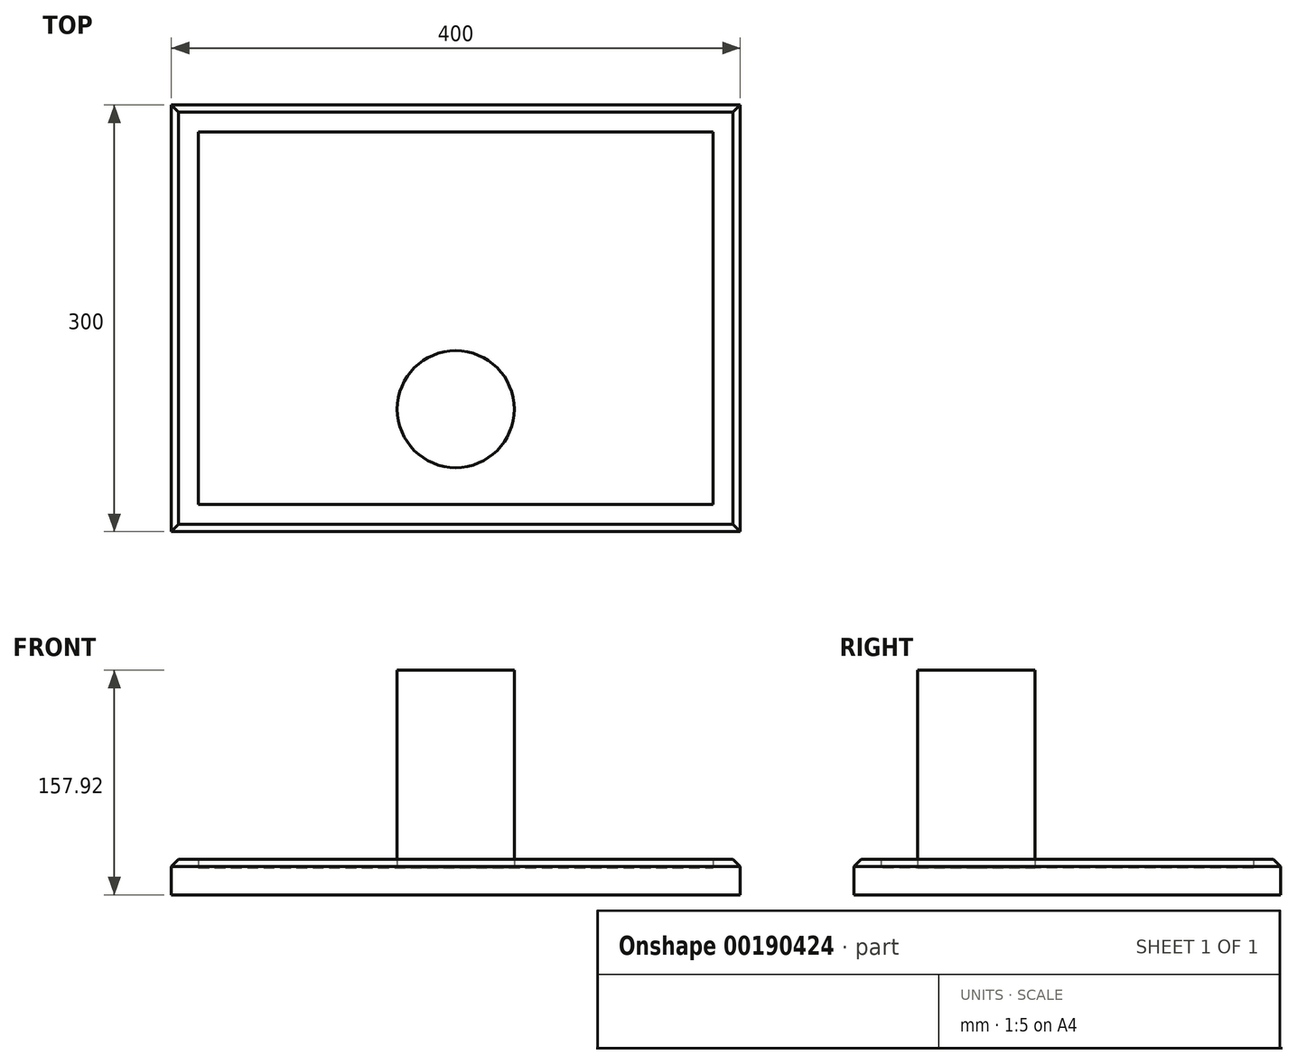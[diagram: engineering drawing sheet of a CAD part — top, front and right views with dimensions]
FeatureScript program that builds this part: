
annotation { "Feature Type Name" : "Feature", "Feature Type Description" : "" }
export const myFeature = defineFeature(function(context is Context, id is Id, definition is map)
    precondition{}
    {
        {
            var Q0;
            Q0=qCreatedBy(makeId("Top.planeOp"),FACE);
            var sketch = newSketch(context, id + "F0", { "sketchPlane" : qUnion([Q0])});
            skLineSegment(sketch, "E0.bottom", {"start": v(-200, 150) * mm, "end": v(200, 150) * mm});
            skLineSegment(sketch, "E0.top", {"start": v(-200, -150) * mm, "end": v(200, -150) * mm});
            skLineSegment(sketch, "E0.left", {"start": v(-200, 150) * mm, "end": v(-200, -150) * mm});
            skLineSegment(sketch, "E0.right", {"start": v(200, 150) * mm, "end": v(200, -150) * mm});
            skPoint(sketch, "E0.middle", {"position": v(0, 0) * mm});
            skSolve(sketch);
        }
        {
            var Q0;
            Q0 = qSketchRegion(id + "F0", true);
            extrude(context, id + "F1", {"entities" : qUnion([Q0]), "depth" : 25 * mm});
        }
        {
            var Q0;
            Q0=makeQuery(id+"F1.opExtrude","CAP_FACE",FACE,{"disambiguationData":[OSD([sQuery(id+"F0.wireOp",EDGE,"E0.bottom"),sQuery(id+"F0.wireOp",EDGE,"E0.top"),sQuery(id+"F0.wireOp",EDGE,"E0.left"),sQuery(id+"F0.wireOp",EDGE,"E0.right")])],"isStart":false});
            shell(context, id + "F2", {"entities" : qUnion([Q0]), "thickness" : 19 * mm});
        }
        {
            var Q0;
            Q0=makeQuery(id+"F1.opExtrude","CAP_EDGE",EDGE,{"disambiguationData":[OSD([sQuery(id+"F0.wireOp",EDGE,"E0.left")])],"isStart":false});
            var Q1;
            Q1=makeQuery(id+"F1.opExtrude","CAP_EDGE",EDGE,{"disambiguationData":[OSD([sQuery(id+"F0.wireOp",EDGE,"E0.bottom")])],"isStart":false});
            var Q2;
            Q2=makeQuery(id+"F1.opExtrude","CAP_EDGE",EDGE,{"disambiguationData":[OSD([sQuery(id+"F0.wireOp",EDGE,"E0.right")])],"isStart":false});
            var Q3;
            Q3=makeQuery(id+"F1.opExtrude","CAP_EDGE",EDGE,{"disambiguationData":[OSD([sQuery(id+"F0.wireOp",EDGE,"E0.top")])],"isStart":false});
            chamfer(context, id + "F3", {"entities" : qUnion([Q0, Q1, Q2, Q3]), "width" : 5 * mm, "tangentPropagation" : true});
        }
        {
            var Q0;
            Q0=makeQuery(id+"F2.opShell","OFFSET_FACE",FACE,{"disambiguationData":[OSD([sQuery(id+"F0.wireOp",EDGE,"E0.bottom"),sQuery(id+"F0.wireOp",EDGE,"E0.top"),sQuery(id+"F0.wireOp",EDGE,"E0.left"),sQuery(id+"F0.wireOp",EDGE,"E0.right")])]});
            var sketch = newSketch(context, id + "F5", { "sketchPlane" : qUnion([Q0])});
            skCircle(sketch, "E1", {"center": v(0, -63.9) * mm, "radius": 41.15 * mm});
            skSolve(sketch);
        }
        {
            var Q0;
            Q0=makeQuery(id+"F5.imprint","IMPRINT",FACE,{"disambiguationData":[TD([[makeQuery(id+"F5.imprint","IMPRINT",EDGE,{"derivedFrom":sQuery(id+"F5.wireOp",EDGE,"E1")}),1.0]])]});
            extrude(context, id + "F4", {"entities" : qUnion([Q0]), "operationType" : NewBodyOperationType.ADD, "depth" : 138.92 * mm});
        }
    });
